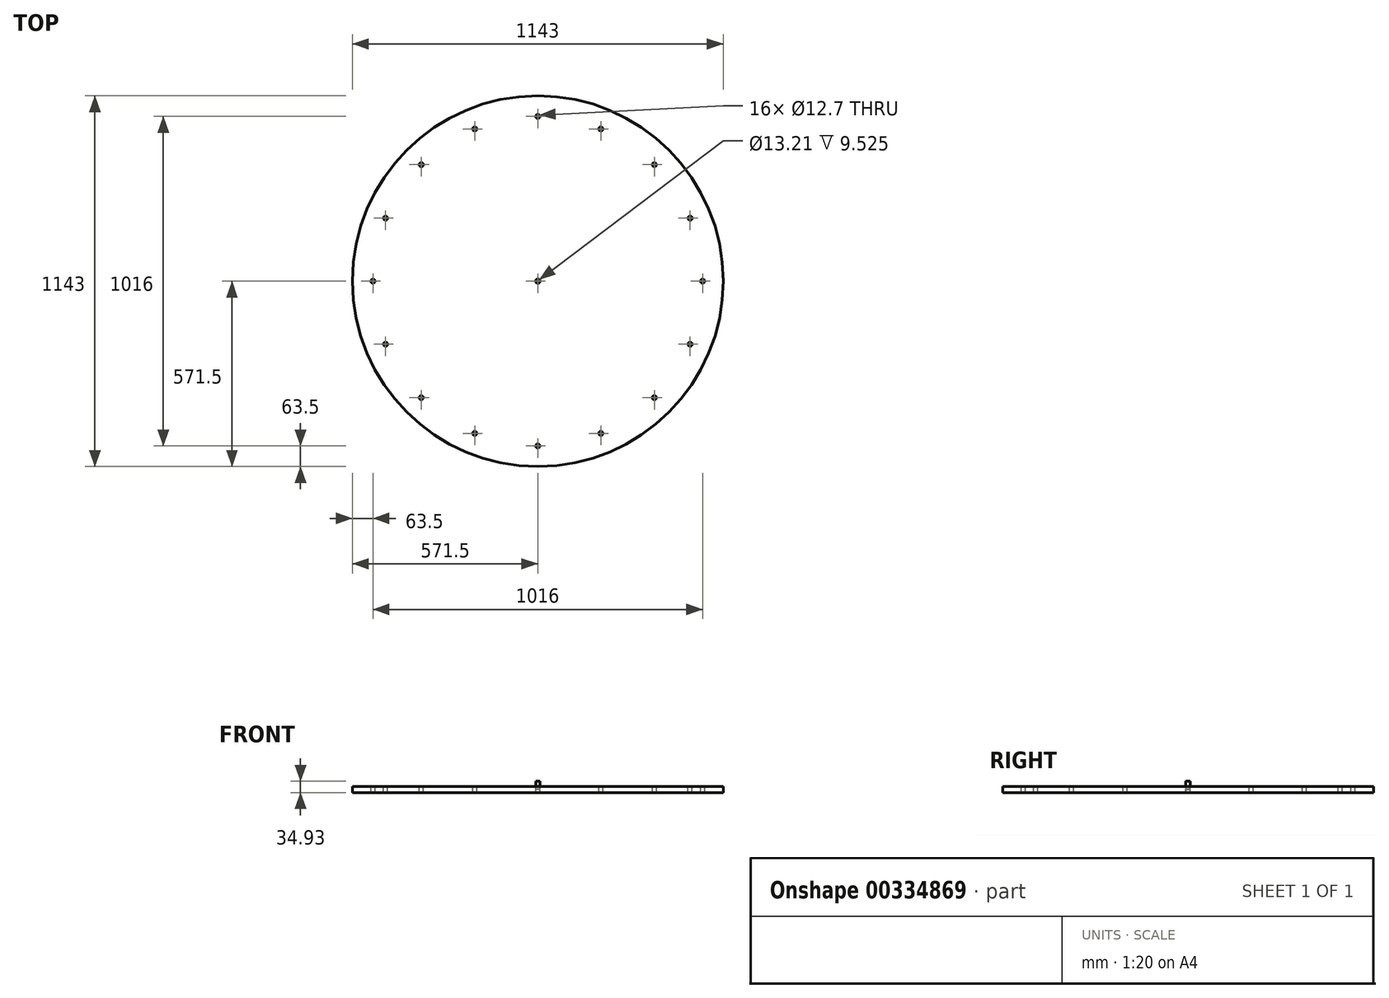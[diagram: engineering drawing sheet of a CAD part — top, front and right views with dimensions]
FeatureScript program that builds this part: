
annotation { "Feature Type Name" : "Feature", "Feature Type Description" : "" }
export const myFeature = defineFeature(function(context is Context, id is Id, definition is map)
    precondition{}
    {
        {
            var Q0;
            Q0=qCreatedBy(makeId("Top.planeOp"),FACE);
            var sketch = newSketch(context, id + "F0", { "sketchPlane" : qUnion([Q0])});
            skCircle(sketch, "E0", {"center": v(0, 0) * mm, "radius": 571.5 * mm});
            skLineSegment(sketch, "E1", {"start": v(0, 571.5) * mm, "end": v(0, -571.5) * mm, "construction": true});
            skCircle(sketch, "E2", {"center": v(0, -508) * mm, "radius": 6.35 * mm});
            skCircle(sketch, "E3.1.0", {"center": v(-194.4, -469.33) * mm, "radius": 6.35 * mm});
            skCircle(sketch, "E3.2.0", {"center": v(-359.21, -359.21) * mm, "radius": 6.35 * mm});
            skCircle(sketch, "E3.3.0", {"center": v(-469.33, -194.4) * mm, "radius": 6.35 * mm});
            skCircle(sketch, "E3.4.0", {"center": v(-508, 0) * mm, "radius": 6.35 * mm});
            skCircle(sketch, "E3.5.0", {"center": v(-469.33, 194.4) * mm, "radius": 6.35 * mm});
            skCircle(sketch, "E3.6.0", {"center": v(-359.21, 359.21) * mm, "radius": 6.35 * mm});
            skCircle(sketch, "E3.7.0", {"center": v(-194.4, 469.33) * mm, "radius": 6.35 * mm});
            skLineSegment(sketch, "E3.anchor1", {"start": v(0, 0) * mm, "end": v(0, -508) * mm, "construction": true});
            skLineSegment(sketch, "E3.anchor2", {"start": v(0, 0) * mm, "end": v(0, 508) * mm, "construction": true});
            skCircle(sketch, "E4.1.8.0", {"center": v(0, 508) * mm, "radius": 6.35 * mm});
            skCircle(sketch, "E5.2.0", {"center": v(194.4, 469.33) * mm, "radius": 6.35 * mm});
            skCircle(sketch, "E5.3.0", {"center": v(359.21, 359.21) * mm, "radius": 6.35 * mm});
            skCircle(sketch, "E5.4.0", {"center": v(469.33, 194.4) * mm, "radius": 6.35 * mm});
            skCircle(sketch, "E5.5.0", {"center": v(508, 0) * mm, "radius": 6.35 * mm});
            skCircle(sketch, "E5.6.0", {"center": v(469.33, -194.4) * mm, "radius": 6.35 * mm});
            skCircle(sketch, "E5.7.0", {"center": v(359.21, -359.21) * mm, "radius": 6.35 * mm});
            skCircle(sketch, "E5.8.0", {"center": v(194.4, -469.33) * mm, "radius": 6.35 * mm});
            skCircle(sketch, "E6", {"center": v(0, 0) * mm, "radius": 6.6 * mm});
            skSolve(sketch);
        }
        {
            var Q0;
            Q0=makeQuery(id+"F0.imprint","IMPRINT",FACE,{"disambiguationData":[TD([[makeQuery(id+"F0.imprint","IMPRINT",EDGE,{"derivedFrom":sQuery(id+"F0.wireOp",EDGE,"E0")}),1.0]])]});
            extrude(context, id + "F1", {"entities" : qUnion([Q0]), "oppositeDirection" : true, "depth" : 19.05 * mm});
        }
        {
            var Q0;
            Q0=makeQuery(id+"F0.imprint","IMPRINT",FACE,{"disambiguationData":[TD([[makeQuery(id+"F0.imprint","IMPRINT",EDGE,{"derivedFrom":sQuery(id+"F0.wireOp",EDGE,"E6")}),1.0]])]});
            extrude(context, id + "F2", {"entities" : qUnion([Q0]), "operationType" : NewBodyOperationType.ADD, "endBound" : BoundingType.SYMMETRIC, "depth" : 19.05 * mm});
        }
        {
            var Q0;
            Q0=makeQuery(id+"F2.opExtrude","CAP_FACE",FACE,{"disambiguationData":[OSD([sQuery(id+"F0.wireOp",EDGE,"E6")])],"isStart":false});
            extrude(context, id + "F3", {"entities" : qUnion([Q0]), "operationType" : NewBodyOperationType.ADD, "depth" : 6.35 * mm});
        }
    });
